FCSTD DOCUMENT  (FreeCAD 0.19R24267 +148 (Git))
Label: Bottom Angle - Small
License: All rights reserved
LicenseURL: http://en.wikipedia.org/wiki/All_rights_reserved
objects: Part::Feature×1, Part::FeaturePython×1, App::MeasureDistance×1, PartDesign::FeatureBase×1, PartDesign::Body×1
note: 4 computed .brp shape members not serialized (recipe doc carries the construction recipe); baked Part::Feature solids carry a one-line shape summary decoded from their .brp

FEATURE [Part::Feature] Bottom_angle001_solid  label="Bottom_angle001 (Solid)"
  shape: bbox 35 x 35 x 15 mm, 15534 faces (baked)
FEATURE [Part::FeaturePython] Clone  label="Bottom_angle001 (Solid)001"  # Draft clone (typed FeaturePython)
  AttacherType = Attacher::AttachEngine3D
  Fuse = false
  Objects = -> [Bottom_angle001_solid]
  Placement = pos=(69,0,0) rot=(0,0,1;0rad)
  Scale = (0.6,0.6,0.6)
FEATURE [App::MeasureDistance] Distance  label="Distance: 1.80 mm"
  Distance = 1.79974
  P1 = (249.302,4.13723,11.4)
  P2 = (251.099,4.23142,11.4)
FEATURE [PartDesign::FeatureBase] BaseFeature
  BaseFeature = -> Clone
FEATURE [PartDesign::Body] Body
  BaseFeature = -> Clone
  Group = -> [BaseFeature]
  Origin = -> Origin
  Tip = -> BaseFeature
